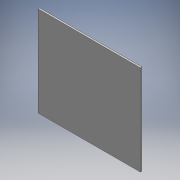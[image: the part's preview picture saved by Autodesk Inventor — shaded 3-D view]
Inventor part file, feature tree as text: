
AUTODESK INVENTOR PART (.ipt)
format: ipt  version: 2016 (Build 200138000, 138)  size: 84,992 bytes
history: native  units: mm
features: other x1, extrude x1, sketch x1
ambient origin geometry x8: Origin, YZ Plane, XZ Plane, XY Plane, X Axis, Y Axis, Z Axis, Center Point
bodies: Body1 (feature_tree)
feature tree (3):
  other  "ソリッド1"
  extrude  "押し出し1"  Depth=136.0mm
  sketch  "スケッチ1"
